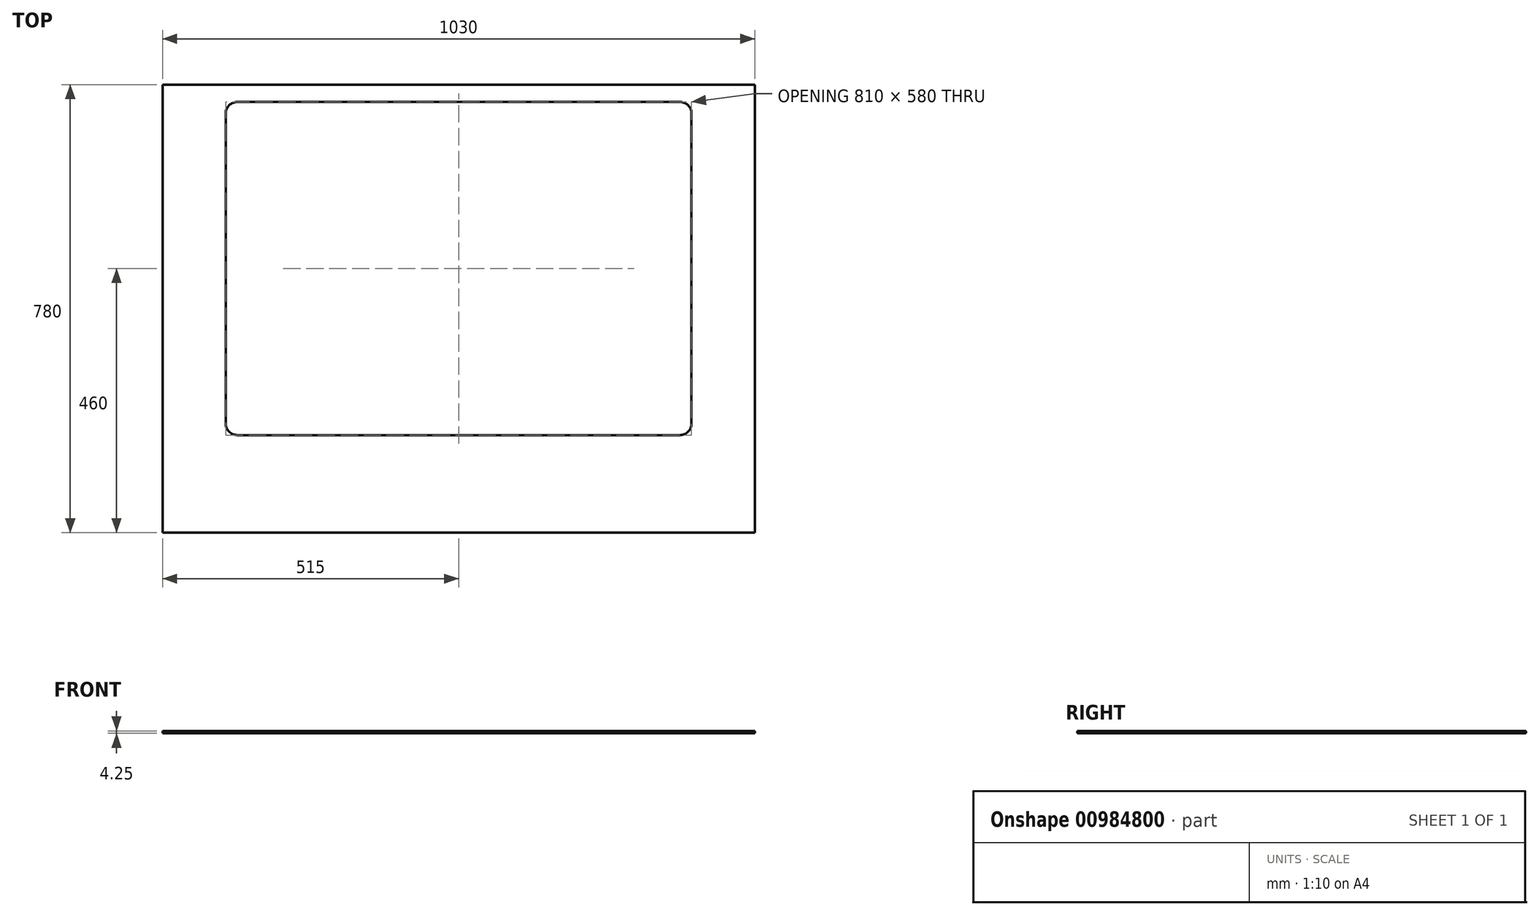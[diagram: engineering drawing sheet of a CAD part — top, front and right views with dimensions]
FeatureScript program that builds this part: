
annotation { "Feature Type Name" : "Feature", "Feature Type Description" : "" }
export const myFeature = defineFeature(function(context is Context, id is Id, definition is map)
    precondition{}
    {
        {
            var Q0;
            Q0=qCreatedBy(makeId("Top.planeOp"),FACE);
            var sketch = newSketch(context, id + "F0", { "sketchPlane" : qUnion([Q0])});
            skLineSegment(sketch, "E0.bottom", {"start": v(-515, 390) * mm, "end": v(515, 390) * mm});
            skLineSegment(sketch, "E0.top", {"start": v(-515, -390) * mm, "end": v(515, -390) * mm});
            skLineSegment(sketch, "E0.left", {"start": v(-515, 390) * mm, "end": v(-515, -390) * mm});
            skLineSegment(sketch, "E0.right", {"start": v(515, 390) * mm, "end": v(515, -390) * mm});
            skPoint(sketch, "E0.middle", {"position": v(0, 0) * mm});
            skSolve(sketch);
        }
        {
            var Q0;
            Q0=qSketchRegion(id+"F0",true);
            extrude(context, id + "F1", {"entities" : qUnion([Q0]), "depth" : 4.25 * mm, "offsetDistance" : 25.4 * mm});
        }
        {
            var Q0;
            Q0=makeQuery(id+"F1.opExtrude","CAP_FACE",FACE,{"disambiguationData":[OSD([sQuery(id+"F0.wireOp",EDGE,"E0.bottom"),sQuery(id+"F0.wireOp",EDGE,"E0.top"),sQuery(id+"F0.wireOp",EDGE,"E0.left"),sQuery(id+"F0.wireOp",EDGE,"E0.right")])],"isStart":false});
            var sketch = newSketch(context, id + "F2", { "sketchPlane" : qUnion([Q0])});
            skLineSegment(sketch, "E1.bottom", {"start": v(-405, 360) * mm, "end": v(405, 360) * mm});
            skLineSegment(sketch, "E1.top", {"start": v(-405, -220) * mm, "end": v(405, -220) * mm});
            skLineSegment(sketch, "E1.left", {"start": v(-405, 360) * mm, "end": v(-405, -220) * mm});
            skLineSegment(sketch, "E1.right", {"start": v(405, 360) * mm, "end": v(405, -220) * mm});
            skLineSegment(sketch, "E2", {"start": v(0, 0) * mm, "end": v(0, 390) * mm, "construction": true});
            skSolve(sketch);
        }
        {
            var Q0;
            Q0=qSketchRegion(id+"F2",true);
            extrude(context, id + "F3", {"entities" : qUnion([Q0]), "operationType" : NewBodyOperationType.REMOVE, "endBound" : BoundingType.UP_TO_NEXT, "oppositeDirection" : true, "depth" : 25.4 * mm, "offsetDistance" : 25.4 * mm});
        }
        {
            var Q0;
            Q0=makeQuery(id+"F3.boolean.opBoolean","COPY",EDGE,{"derivedFrom":makeQuery(id+"F3.opExtrude","SWEPT_EDGE",EDGE,{"disambiguationData":[OSD([sQuery(id+"F2.wireOp",EDGE,"E1.bottom"),sQuery(id+"F2.wireOp",EDGE,"E1.right")])]})});
            var Q1;
            Q1=makeQuery(id+"F3.boolean.opBoolean","COPY",EDGE,{"derivedFrom":makeQuery(id+"F3.opExtrude","SWEPT_EDGE",EDGE,{"disambiguationData":[OSD([sQuery(id+"F2.wireOp",EDGE,"E1.top"),sQuery(id+"F2.wireOp",EDGE,"E1.right")])]})});
            var Q2;
            Q2=makeQuery(id+"F3.boolean.opBoolean","COPY",EDGE,{"derivedFrom":makeQuery(id+"F3.opExtrude","SWEPT_EDGE",EDGE,{"disambiguationData":[OSD([sQuery(id+"F2.wireOp",EDGE,"E1.top"),sQuery(id+"F2.wireOp",EDGE,"E1.left")])]})});
            var Q3;
            Q3=makeQuery(id+"F3.boolean.opBoolean","COPY",EDGE,{"derivedFrom":makeQuery(id+"F3.opExtrude","SWEPT_EDGE",EDGE,{"disambiguationData":[OSD([sQuery(id+"F2.wireOp",EDGE,"E1.bottom"),sQuery(id+"F2.wireOp",EDGE,"E1.left")])]})});
            fillet(context, id + "F4", {"entities" : qUnion([Q0, Q1, Q2, Q3]), "radius" : 20 * mm, "tangentPropagation" : true, "allowEdgeOverflow" : false});
        }
        {
            var Q0;
            Q0=makeQuery(id+"F1.opExtrude","CAP_FACE",FACE,{"disambiguationData":[OSD([sQuery(id+"F0.wireOp",EDGE,"E0.bottom"),sQuery(id+"F0.wireOp",EDGE,"E0.top"),sQuery(id+"F0.wireOp",EDGE,"E0.left"),sQuery(id+"F0.wireOp",EDGE,"E0.right")])],"isStart":false});
            var sketch = newSketch(context, id + "F5", { "sketchPlane" : qUnion([Q0])});
            skLineSegment(sketch, "E3", {"start": v(0, 360) * mm, "end": v(0, -220) * mm, "construction": true});
            skLineSegment(sketch, "E4", {"start": v(-405, 70) * mm, "end": v(405, 70) * mm, "construction": true});
            skSolve(sketch);
        }
    });
